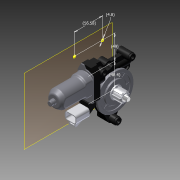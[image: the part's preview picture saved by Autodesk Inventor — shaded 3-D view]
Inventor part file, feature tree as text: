
AUTODESK INVENTOR PART (.ipt)
format: ipt  version: 2014 SP1 (Build 180222100, 222)  size: 1,737,216 bytes
history: native  units: mm (DEFAULTED — no unit token found)
features: sketch x60, extrude x51, fillet x11, chamfer x9, hole x6, pattern_circular x4, plane x3, revolve x2, other x1, mirror x1, projected_geometry x1
ambient origin geometry x8: Origin, YZ Plane, XZ Plane, XY Plane, X Axis, Y Axis, Z Axis, Center Point
bodies: Solid1 (feature_tree)
feature tree (149):
  extrude  "Extrusion1"  Depth=5.0mm TaperAngle=0.0deg
  extrude  "Extrusion2"  Depth=42.0mm
  extrude  "Extrusion3"  Depth=2.0mm
  extrude  "Extrusion4"  Depth=1.0mm
  extrude  "Extrusion5"  Depth=4.0mm
  pattern_circular  "Circular Pattern1"  Count=8 Angle=360.0deg
  extrude  "Extrusion6"  Depth=1.7mm TaperAngle=0.0deg
  extrude  "Extrusion7"  Depth=17.9mm TaperAngle=0.0deg
  hole  "Hole1"  [1 undecoded]
  extrude  "Extrusion8"  Depth=18.0mm TaperAngle=0.0deg
  chamfer  "Chamfer1"  Distance=2.0mm
  pattern_circular  "Circular Pattern2"  Count=6 Angle=360.0deg
  extrude  "Extrusion9"  Depth=12.5mm TaperAngle=0.0deg
  extrude  "Extrusion10"  Depth=2.0mm TaperAngle=0.0deg
  chamfer  "Chamfer2"  Distance=2.0mm
  fillet  "Fillet1"  Radius=0.5mm
  fillet  "Fillet2"  Radius=1.5mm
  extrude  "Extrusion11"  Depth=0.5mm TaperAngle=0.0deg
  extrude  "Extrusion12"  Depth=3.0mm
  extrude  "Extrusion13"  Depth=2.0mm
  revolve  "Revolution1"  [1 undecoded]
  extrude  "Extrusion14"  TaperAngle=30.0deg  [1 undecoded]
  pattern_circular  "Circular Pattern3"  Count=12 Angle=360.0deg
  extrude  "Extrusion15"  Depth=0.5mm
  fillet  "Fillet3"  Radius=43.0mm
  extrude  "Extrusion16"  Depth=2.0mm TaperAngle=0.0deg
  fillet  "Fillet4"  Radius=1.0mm
  hole  "Hole2"  [1 undecoded]
  extrude  "Extrusion18"  Depth=0.9mm
  fillet  "Fillet5"  Radius=120.0mm
  pattern_circular  "Circular Pattern4"  Count=2  [1 undecoded]
  plane  "Work Plane1"
  plane  "Work Plane2"
  other  "Work Axis1"
  extrude  "Extrusion19"  Depth=23.0mm
  extrude  "Extrusion20"  Depth=5.0mm TaperAngle=0.0deg
  extrude  "Extrusion21"  Depth=31.0mm
  extrude  "Extrusion22"  Depth=4.0mm
  extrude  "Extrusion23"  Depth=6.0mm
  fillet  "Fillet6"  Radius=0.2mm
  chamfer  "Chamfer3"  Distance=2.0mm
  chamfer  "Chamfer4"  Distance=15.0mm
  extrude  "Extrusion24"  Depth=17.5mm
  fillet  "Fillet7"  Radius=40.0mm
  extrude  "Extrusion25"  Depth=1.0mm
  extrude  "Extrusion26"  TaperAngle=90.0deg  [1 undecoded]
  chamfer  "Chamfer5"  Distance=43.0mm
  chamfer  "Chamfer6"  Distance=4.0mm
  fillet  "Fillet8"  Radius=9.0mm
  revolve  "Revolution2"  [1 undecoded]
  extrude  "Extrusion27"  Depth=2.0mm TaperAngle=0.0deg
  mirror  "Mirror1"
  fillet  "Fillet9"  Radius=13.2mm
  extrude  "Extrusion28"  Depth=18.0mm TaperAngle=0.0deg
  extrude  "Extrusion29"  Depth=7.0mm
  fillet  "Fillet10"  Radius=50.0mm
  extrude  "Extrusion30"  Depth=14.0mm
  extrude  "Extrusion31"  Depth=8.2mm TaperAngle=0.0deg
  chamfer  "Chamfer8"  Distance=3.0mm
  extrude  "Extrusion32"  Depth=2.0mm
  extrude  "Extrusion33"  Depth=2.0mm TaperAngle=0.0deg
  extrude  "Extrusion34"  Depth=7.0mm
  hole  "Hole3"  [1 undecoded]
  extrude  "Extrusion35"  Depth=3.0mm TaperAngle=0.0deg
  extrude  "Extrusion36"  Depth=15.5mm
  extrude  "Extrusion39"  Depth=5.0mm
  extrude  "Extrusion40"  Depth=2.0mm
  extrude  "Extrusion41"  Depth=16.0mm TaperAngle=0.0deg
  hole  "Hole4"  [1 undecoded]
  extrude  "Extrusion42"  Depth=2.0mm
  extrude  "Extrusion43"  Depth=2.0mm
  extrude  "Extrusion46"  Depth=9.5mm TaperAngle=0.0deg
  extrude  "Extrusion47"  Depth=2.0mm
  extrude  "Extrusion48"  Depth=2.0mm
  hole  "Hole5"  [1 undecoded]
  hole  "Hole6"  [1 undecoded]
  extrude  "Extrusion50"  Depth=3.0mm TaperAngle=0.0deg
  extrude  "Extrusion51"  Depth=2.0mm
  extrude  "Extrusion52"  Depth=2.0mm TaperAngle=0.0deg
  extrude  "Extrusion53"  Depth=2.0mm TaperAngle=0.0deg
  chamfer  "Chamfer9"  Distance=2.0mm
  extrude  "Extrusion55"  Depth=13.0mm TaperAngle=0.0deg
  fillet  "Fillet12"  Radius=18.5mm
  extrude  "Extrusion56"  Depth=9.0mm
  extrude  "Extrusion57"  Depth=2.0mm
  chamfer  "Chamfer10"  Distance=15.0mm
  extrude  "Extrusion59"  Depth=19.0mm
  plane  "Work Plane3"
  sketch  "Sketch73"  dims[d207=4.8mm d208=6.0mm d209=6.2mm d210=2.0mm d211=14.3117mm d212=8.0mm d213=0.0mm d214=15.5mm d215=5.0mm d216=41.0mm d217=16.0mm d218=0.0mm d219=9.0mm d220=3.5mm d221=6.25mm d222=9.5mm d223=0.0mm d230=14.2mm d231=48.4mm d232=14.8mm d233=0.0mm d234=12.3mm d235=3.0mm d236=0.0mm d237=16.5mm d238=17.5mm d239=0.0mm d240=4.8mm d241=6.0mm d242=6.2mm d243=2.0mm d244=14.3117mm d245=28.0mm d246=20.594885mm d247=4.134mm d248=6.0mm d249=4.9mm d250=2.0mm d251=14.3117mm d252=8.0mm d253=0.0mm d259=2.0mm d260=0.0mm d261=2.0mm d262=0.0mm d263=13.0mm d264=0.0mm d270=18.5mm d271=0.0mm d272=9.0mm d273=13.0mm d280=2.0mm d281=15.0mm d282=19.0mm d284=23.0mm d285=15.5mm d286=7.5mm d287=27.3mm d288=0.0mm d289=5.0mm d290=1.6mm d291=24.3mm d292=0.0mm d293=13.8mm d294=3.0mm d295=7.0mm d296=0.0mm d302=5.0mm d303=10.0mm d304=9.0mm d305=2.0mm d306=12.5mm d307=0.0mm d308=20.0mm d309=2.0mm d310=2.0mm d311=45.0deg d312=45.0deg d313=45.0deg d314=45.0deg d315=45.0deg d316=45.0deg d317=45.0deg d318=45.0deg d319=45.0deg d320=-50.0mm d321=48.4mm d322=49.0mm d323=56.58mm d324=4.8mm]
  sketch  "Sketch1"  dims[d0=72.0mm d1=5.0mm d2=0.0mm]
  sketch  "Sketch2"  dims[d3=60.0mm d4=42.0mm]
  sketch  "Sketch3"  dims[d5=2.0mm d6=0.0mm d7=2.0mm]
  sketch  "Sketch4"  dims[d8=1.0mm d9=0.0mm d10=26.0mm]
  sketch  "Sketch5"  dims[d11=0.5mm d12=0.0mm d13=4.0mm]
  sketch  "Sketch6"  dims[d14=8.0mm]
  sketch  "Sketch7"  dims[d15=22.0mm]
  sketch  "Sketch8"  dims[d16=1.5mm d17=0.0mm]
  sketch  "Sketch9"  dims[d18=2.0mm d19=80.0mm d21=360.0deg]
  sketch  "Sketch10"  dims[d22=23.9mm d23=1.7mm d24=0.0mm]
  sketch  "Sketch11"  dims[d25=16.2mm d26=17.9mm d27=0.0mm]
  sketch  "Sketch12"  dims[d28=13.0mm d29=6.0mm d30=4.0mm d31=2.0mm d32=14.3117mm d33=2.0mm d34=0.0mm d35=4.0mm]
  sketch  "Sketch13"  dims[d36=10.0mm d37=18.0mm d38=0.0mm d39=2.0mm d40=2.0mm d41=60.0mm d43=360.0deg]
  sketch  "Sketch14"  dims[d44=12.5mm d45=0.2mm d46=0.0mm]
  sketch  "Sketch15"  dims[d47=8.0mm d48=8.2mm d49=0.0mm d50=0.5mm d51=2.0mm d52=0.5mm d53=1.5mm]
  sketch  "Sketch16"  dims[d54=71.0mm d55=0.5mm d56=0.0mm]
  sketch  "Sketch17"  dims[d57=3.0mm d58=0.0mm d59=68.0mm]
  sketch  "Sketch18"  dims[d60=14.0mm d61=0.0mm d62=2.0mm]
  sketch  "Sketch19"  dims[d63=3.5mm d64=10.0mm]
  sketch  "Sketch21"  dims[d65=90.0deg d66=30.0deg]
  sketch  "Sketch22"  dims[d67=1.0mm]
  sketch  "Sketch23"  dims[d68=1.0mm]
  sketch  "Sketch24"  dims[d69=4.5mm d70=0.0mm d71=120.0mm d73=360.0deg]
  sketch  "Sketch25"  dims[d74=0.5mm d75=0.0mm d76=0.5mm d77=43.0mm]
  sketch  "Sketch26"  dims[d78=2.0mm d79=2.0mm d80=0.0mm d81=1.0mm]
  sketch  "Sketch27"  dims[d82=2.6mm d83=6.0mm d84=4.0mm d85=2.0mm d86=14.3117mm d87=8.0mm d88=0.0mm d93=2.0mm]
  sketch  "Sketch28"  dims[d94=15.5mm d95=0.0mm d96=0.9mm d97=120.0mm d99=360.0deg]
  sketch  "Sketch29"  dims[d100=-12.0mm d101=-33.88mm]
  sketch  "Sketch30"  dims[d102=15.0mm]
  projected_geometry  "Projected Loop1"
  sketch  "Sketch31"  dims[d103=35.0mm d104=0.0mm d105=20.0mm d106=0.0mm]
  sketch  "Sketch32"  dims[d108=14.5mm d109=0.0mm d110=23.0mm]
  sketch  "Sketch33"  dims[d111=12.25mm d112=5.0mm d113=0.0mm]
  sketch  "Sketch35"  dims[d114=60.0mm d115=31.0mm]
  sketch  "Sketch36"  dims[d116=12.5mm d117=0.0mm d118=4.0mm]
  sketch  "Sketch37"  dims[d119=12.0mm d120=6.0mm d121=6.0mm d122=12.0mm d123=0.2mm]
  sketch  "Sketch38"  dims[d124=0.2mm]
  sketch  "Sketch39"  dims[d125=0.2mm]
  sketch  "Sketch40"  dims[d126=120.0deg d127=2.0mm d128=0.0mm]
  sketch  "Sketch41"  dims[d129=1.0mm]
  sketch  "Sketch43"  dims[d130=40.0mm d131=15.0mm d132=0.0mm]
  sketch  "Sketch46"  dims[d133=35.0mm d134=17.5mm d135=40.0mm d136=0.0mm]
  sketch  "Sketch47"  dims[d137=2.5mm d138=12.0mm d139=1.0mm d140=12.0mm]
  sketch  "Sketch48"  dims[d143=4.0mm d144=90.0deg d145=43.0mm d146=0.0mm]
  sketch  "Sketch49"  dims[d147=8.0mm]
  sketch  "Sketch50"  dims[d148=12.0mm]
  sketch  "Sketch51"  dims[d149=4.0mm]
  sketch  "Sketch54"  dims[d150=10.0mm d151=4.0mm d152=0.0mm d153=9.0mm]
  sketch  "Sketch55"  dims[d154=5.0mm d155=0.0mm d156=1.0mm]
  sketch  "Sketch56"  dims[d157=0.5mm d158=2.0mm d159=0.0mm d160=13.2mm]
  sketch  "Sketch57"  dims[d161=30.0mm d162=18.0mm d163=0.0mm]
  sketch  "Sketch58"  dims[d164=9.0mm d165=14.0mm d166=7.0mm d167=50.0mm d168=0.0mm]
  sketch  "Sketch60"  dims[d169=14.88mm d170=14.0mm]
  sketch  "Sketch61"  dims[d171=20.71mm d172=8.2mm d173=0.0mm]
  sketch  "Sketch63"  dims[d174=12.3mm d175=3.0mm d176=0.0mm]
  sketch  "Sketch66"  dims[d177=4.8mm d178=6.0mm d179=6.2mm d180=2.0mm d181=14.3117mm d182=8.0mm d183=0.0mm d184=22.68928mm]
  sketch  "Sketch68"  dims[d185=4.0mm d186=2.0mm d187=0.0mm]
  sketch  "Sketch69"  dims[d191=7.0mm d192=0.0mm d199=56.58mm]
  sketch  "Sketch70"  dims[d200=14.8mm d201=0.0mm d202=12.3mm]
  sketch  "Sketch72"  dims[d203=3.0mm d204=0.0mm d205=8.0mm d206=0.0mm]
note: 11 required parameter values undecoded (feature->parameter linkage not recoverable at this tier; creation-order binding heuristic only, values carry confidence <= 0.55)